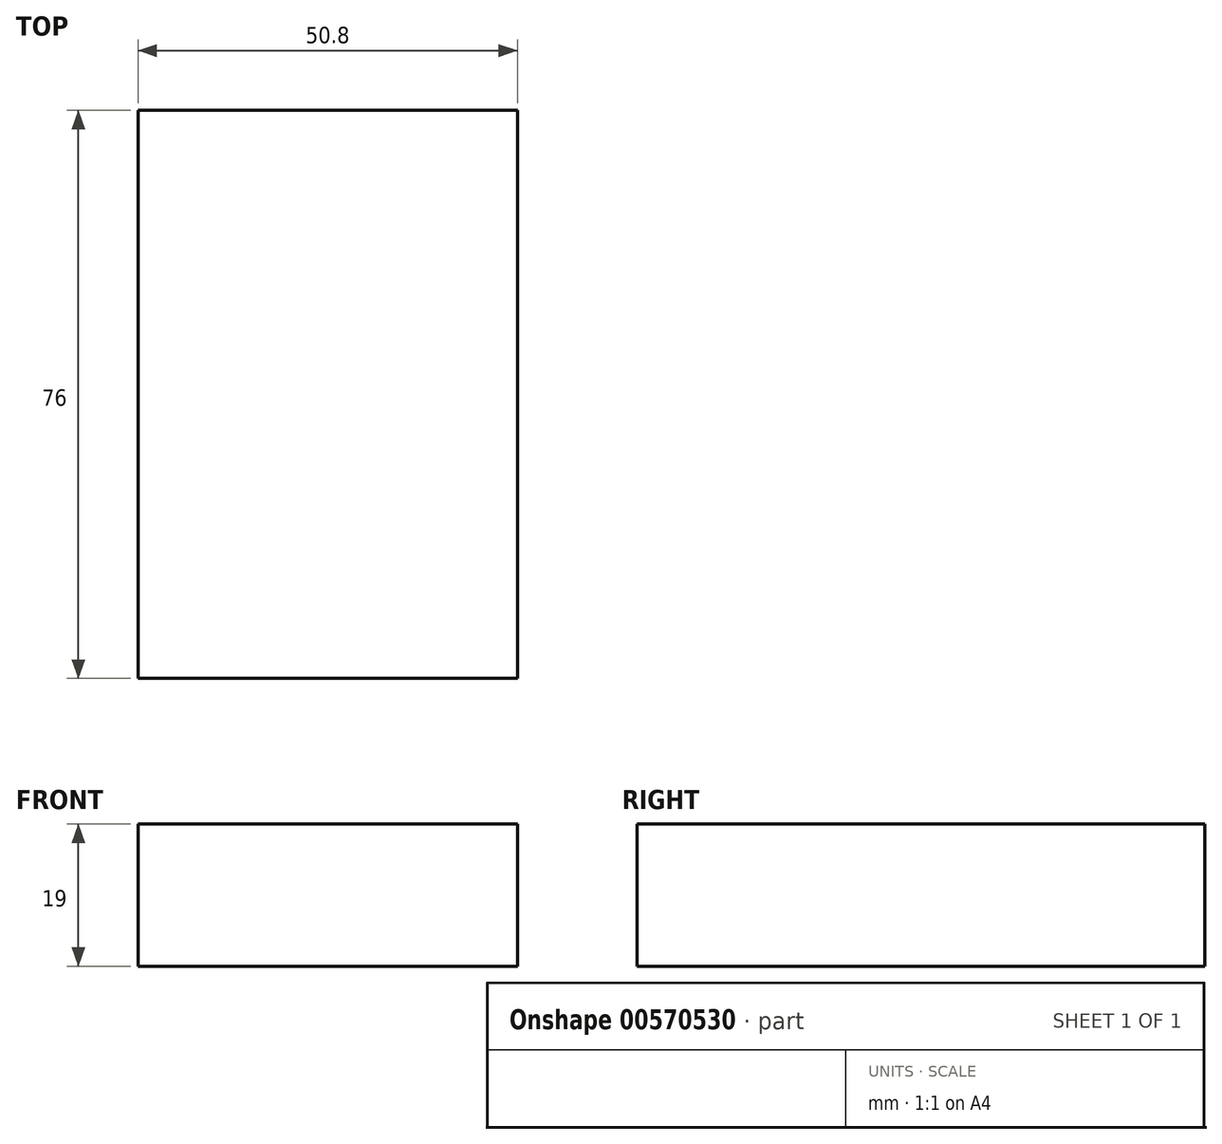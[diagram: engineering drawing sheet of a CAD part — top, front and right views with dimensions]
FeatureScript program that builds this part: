
annotation { "Feature Type Name" : "Feature", "Feature Type Description" : "" }
export const myFeature = defineFeature(function(context is Context, id is Id, definition is map)
    precondition{}
    {
        {
            var Q0;
            Q0=qCreatedBy(makeId("Top.planeOp"),FACE);
            var sketch = newSketch(context, id + "F0", { "sketchPlane" : qUnion([Q0])});
            skLineSegment(sketch, "E0.bottom", {"start": v(25.4, -38) * mm, "end": v(-25.4, -38) * mm});
            skLineSegment(sketch, "E0.top", {"start": v(25.4, 38) * mm, "end": v(-25.4, 38) * mm});
            skLineSegment(sketch, "E0.left", {"start": v(25.4, -38) * mm, "end": v(25.4, 38) * mm});
            skLineSegment(sketch, "E0.right", {"start": v(-25.4, -38) * mm, "end": v(-25.4, 38) * mm});
            skPoint(sketch, "E0.middle", {"position": v(0, 0) * mm});
            skSolve(sketch);
        }
        {
            var Q0;
            Q0=makeQuery(id+"F0.imprint","IMPRINT",FACE,{"disambiguationData":[TD([[makeQuery(id+"F0.imprint","IMPRINT",EDGE,{"derivedFrom":sQuery(id+"F0.wireOp",EDGE,"E0.bottom")}),-1.0]])]});
            extrude(context, id + "F1", {"entities" : qUnion([Q0]), "depth" : 19 * mm, "offsetDistance" : 25 * mm});
        }
    });
